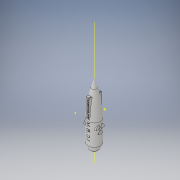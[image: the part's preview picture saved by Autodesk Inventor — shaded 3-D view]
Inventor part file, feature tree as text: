
AUTODESK INVENTOR PART (.ipt)
format: ipt  version: 2018 (Build 220112000, 112)  size: 1,105,920 bytes
history: native  units: in
note: dims shown in document units (in); Inventor stores cm internally (conversion verified against a paired STEP export)
features: sketch x6, other x5, extrude x4, plane x3, revolve x2, chamfer x2, hole x1, fillet x1
ambient origin geometry x8: Origin, YZ Plane, XZ Plane, XY Plane, X Axis, Y Axis, Z Axis, Center Point
bodies: Solid1 (feature_tree)
feature tree (24):
  sketch  "Sketch1"  dims[d3=90.0deg d42=1.0in]
  sketch  "Sketch2"  dims[d43=90.0deg]
  revolve  "Revolution2"  [1 undecoded]
  other  "Work Axis2"
  other  "Work Axis3"
  other  "Work Point2"
  revolve  "Revolution5"  [1 undecoded]
  other  "Work Point3"
  hole  "Hole4"  [1 undecoded]
  plane  "Work Plane9"
  extrude  "Extrusion3"  Depth=0.225in TaperAngle=45.0deg
  plane  "Work Plane10"
  fillet  "Fillet5"  Radius=1.0in
  extrude  "Extrusion4"  [1 undecoded]
  chamfer  "Chamfer1"  [1 undecoded]
  chamfer  "Chamfer2"  [1 undecoded]
  extrude  "Extrusion5"  [1 undecoded]
  extrude  "Extrusion6"  [1 undecoded]
  other  "Work Axis4"
  plane  "Work Plane8"
  sketch  "Sketch6"  dims[d58=1.0in d59=1.0in d47=0.4in d48=0.75in d49=0.375in d50=0.25in d51=0.5635in d52=1.5in d53=60.0deg d54=1.0in d55=0.0in]
  sketch  "Sketch7"  dims[d56=7.75in d57=1.0in d60=0.0in]
  sketch  "Sketch8"  dims[d61=0.225in d62=0.125in d63=45.0deg d64=0.225in d65=0.125in d66=45.0deg d67=1.0in d68=0.0in]
  sketch  "Sketch9"  dims[d69=1.0in d70=0.0in]
note: 8 required parameter values undecoded (feature->parameter linkage not recoverable at this tier; creation-order binding heuristic only, values carry confidence <= 0.55)